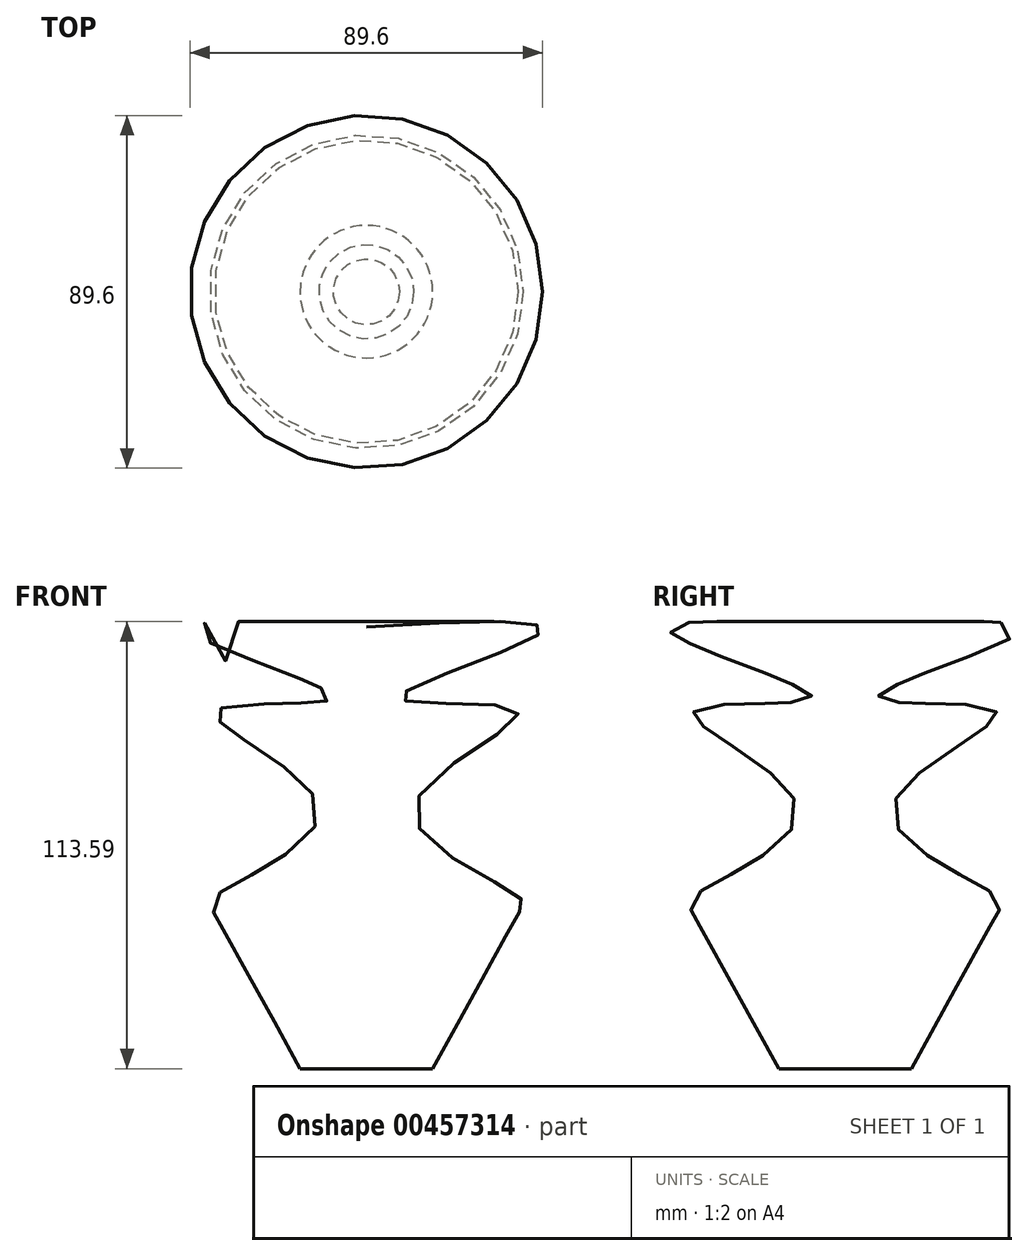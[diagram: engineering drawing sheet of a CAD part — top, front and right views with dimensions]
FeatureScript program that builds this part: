
annotation { "Feature Type Name" : "Feature", "Feature Type Description" : "" }
export const myFeature = defineFeature(function(context is Context, id is Id, definition is map)
    precondition{}
    {
        {
            var Q0;
            Q0=qCreatedBy(makeId("Front.planeOp"),FACE);
            var sketch = newSketch(context, id + "F0", { "sketchPlane" : qUnion([Q0])});
            skLineSegment(sketch, "E0", {"start": v(0, 55.28) * mm, "end": v(0, -57) * mm});
            skLineSegment(sketch, "E1", {"start": v(0, -57) * mm, "end": v(16.84, -57) * mm});
            skPoint(sketch, "E2.5.internal.snap0", {"position": v(8.42, -57) * mm});
            skFitSpline(sketch, "E2", {"points": [v(16.84, -57) * mm, v(38.87, -17.27) * mm, v(38.87, -13.39) * mm, v(12.1, 9.07) * mm, v(38.43, 33.68) * mm, v(8.42, 37.14) * mm, v(44.05, 53.55) * mm, v(0, 55.28) * mm], "startDerivative": vector(160.82, 293.3) * mm, "endDerivative": vector(-435.9, -23.99) * mm});
            skSolve(sketch);
        }
        {
            var Q0;
            Q0=makeQuery(id+"F0.imprint","IMPRINT",FACE,{"disambiguationData":[TD([[makeQuery(id+"F0.imprint","IMPRINT",EDGE,{"derivedFrom":sQuery(id+"F0.wireOp",EDGE,"E0")}),1.0]])]});
            var Q1;
            Q1=sQuery(id+"F0.wireOp",EDGE,"E0");
            revolve(context, id + "F1", {"entities" : qUnion([Q0]), "axis" : qUnion([Q1]), "revolveType" : RevolveType.FULL});
        }
    });
